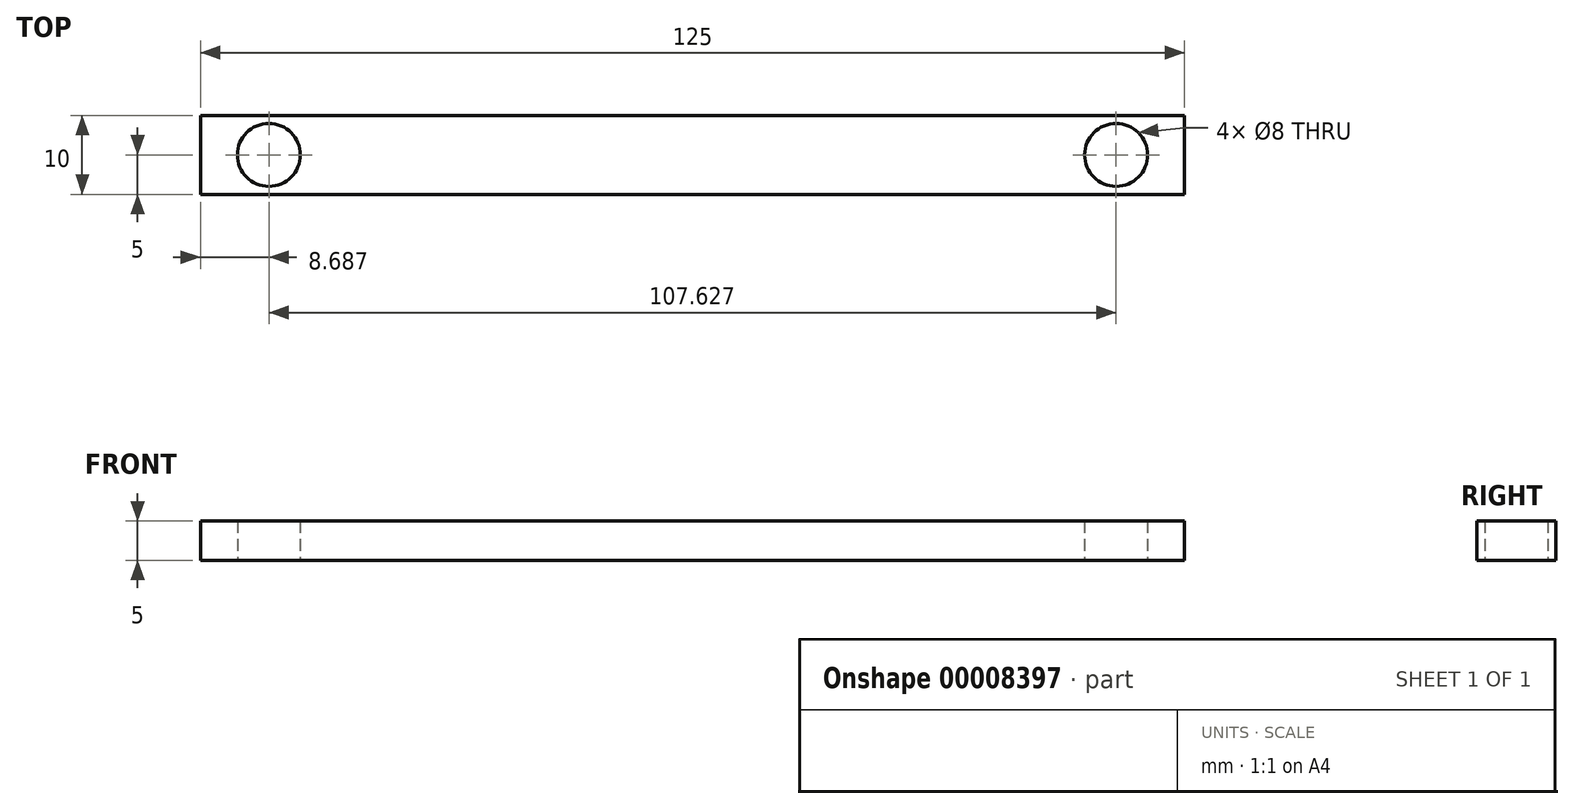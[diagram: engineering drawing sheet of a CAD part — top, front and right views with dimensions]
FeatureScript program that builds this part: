
annotation { "Feature Type Name" : "Feature", "Feature Type Description" : "" }
export const myFeature = defineFeature(function(context is Context, id is Id, definition is map)
    precondition{}
    {
        {
            var Q0;
            Q0=qCreatedBy(makeId("Top.planeOp"),FACE);
            var sketch = newSketch(context, id + "F0", { "sketchPlane" : qUnion([Q0])});
            skLineSegment(sketch, "E0.rect.bottom", {"start": v(-62.5, 5) * mm, "end": v(62.5, 5) * mm});
            skLineSegment(sketch, "E0.rect.top", {"start": v(-62.5, -5) * mm, "end": v(62.5, -5) * mm});
            skLineSegment(sketch, "E0.rect.left", {"start": v(-62.5, 5) * mm, "end": v(-62.5, -5) * mm});
            skLineSegment(sketch, "E0.rect.right", {"start": v(62.5, 5) * mm, "end": v(62.5, -5) * mm});
            skPoint(sketch, "E0.rect.middle", {"position": v(0, 0) * mm});
            skSolve(sketch);
        }
        {
            var Q0;
            Q0=makeQuery(id+"F0.imprint","IMPRINT",FACE,{"disambiguationData":[TD([[makeQuery(id+"F0.imprint","IMPRINT",EDGE,{"derivedFrom":sQuery(id+"F0.wireOp",EDGE,"E0.rect.bottom")}),-1.0]])]});
            extrude(context, id + "F1", {"entities" : qUnion([Q0]), "depth" : 5 * mm});
        }
        {
            var Q0;
            Q0=qCreatedBy(makeId("Top.planeOp"),FACE);
            var sketch = newSketch(context, id + "F2", { "sketchPlane" : qUnion([Q0])});
            skCircle(sketch, "E1", {"center": v(-53.81, 0) * mm, "radius": 4 * mm});
            skCircle(sketch, "E2.0.MirrorC", {"center": v(53.81, 0) * mm, "radius": 4 * mm});
            skSolve(sketch);
        }
        {
            var Q0;
            Q0 = qSketchRegion(id + "F2", true);
            extrude(context, id + "F3", {"entities" : qUnion([Q0]), "operationType" : NewBodyOperationType.REMOVE, "depth" : 25 * mm});
        }
    });
